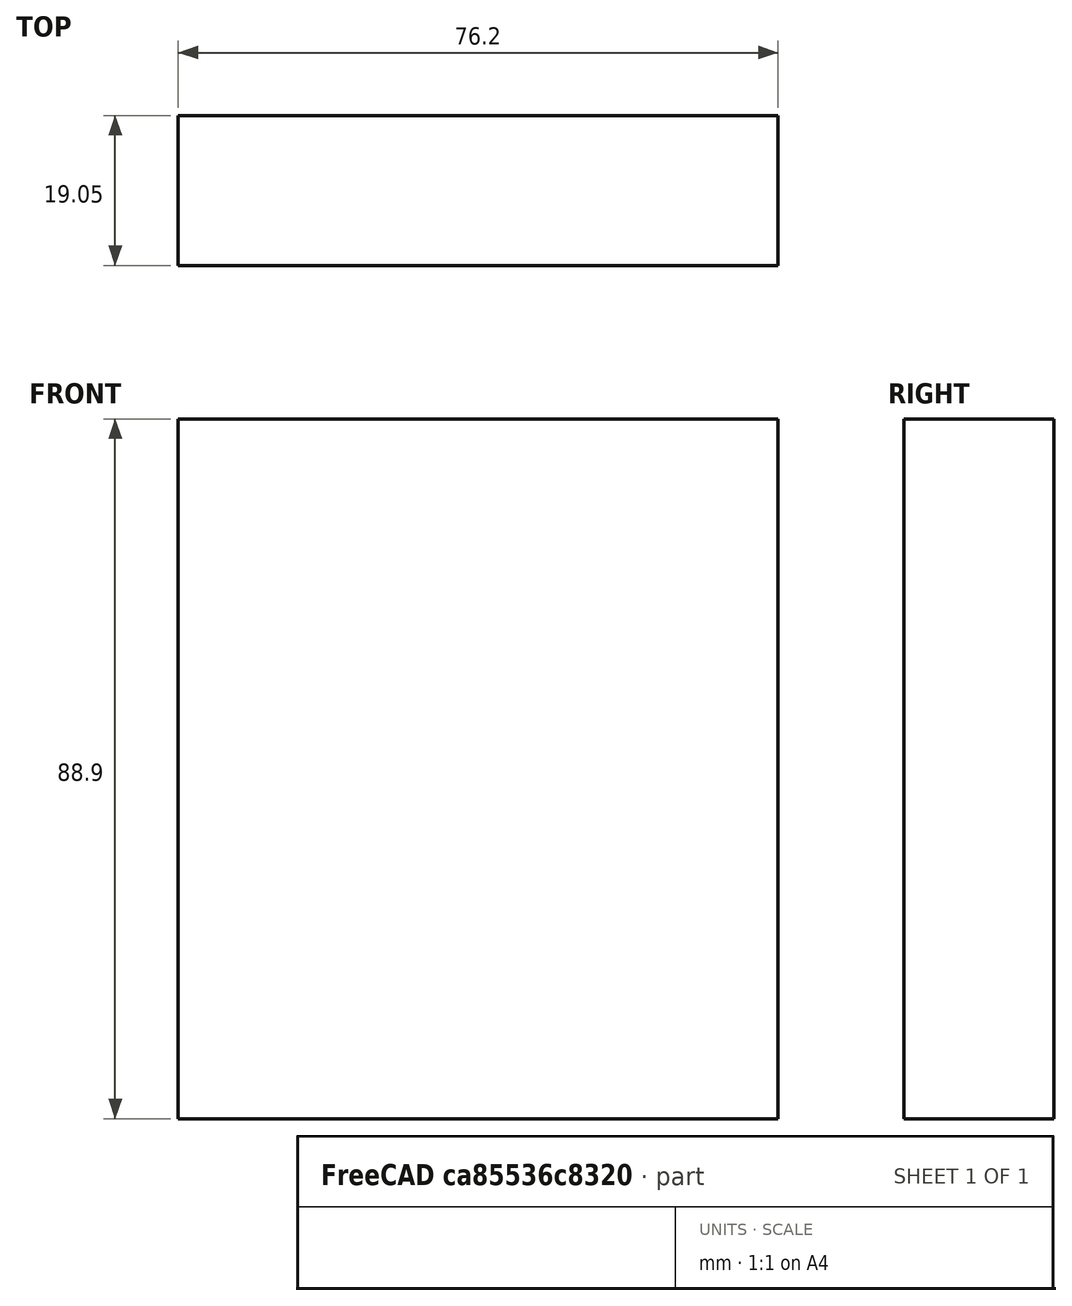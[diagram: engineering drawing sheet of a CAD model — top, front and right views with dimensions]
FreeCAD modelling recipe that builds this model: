
FCSTD DOCUMENT  (FreeCAD 0.20R29603 (Git))
Label: fence_insert
License: All rights reserved
LicenseURL: http://en.wikipedia.org/wiki/All_rights_reserved
objects: TechDraw::DrawProjGroupItem×3, TechDraw::DrawViewDimension×3, Sketcher::SketchObject×1, PartDesign::Pad×1, PartDesign::Body×1, TechDraw::DrawSVGTemplate×1, TechDraw::DrawProjGroup×1, TechDraw::DrawPage×1
note: 4 computed .brp shape members not serialized (recipe doc carries the construction recipe); baked Part::Feature solids carry a one-line shape summary decoded from their .brp

FEATURE [Sketcher::SketchObject] Sketch
  FullyConstrained = true
  MapMode = 5
  Placement = pos=(0,0,0) rot=(1,0,0;1.5708rad)
  Support = -> [XZ_Plane]
  sketch-geometry (5):
    g0: LineSegment StartX=-38.1 StartY=44.45 StartZ=0 EndX=-38.1 EndY=-44.45 EndZ=0
    g1: LineSegment StartX=-38.1 StartY=-44.45 StartZ=0 EndX=38.1 EndY=-44.45 EndZ=0
    g2: LineSegment StartX=38.1 StartY=-44.45 StartZ=0 EndX=38.1 EndY=44.45 EndZ=0
    g3: LineSegment StartX=38.1 StartY=44.45 StartZ=0 EndX=-38.1 EndY=44.45 EndZ=0
    g4: GeomPoint X=0 Y=0 Z=0
  constraints (12):
    c: Coincident(g0,g1)
    c: Coincident(g1,g2)
    c: Coincident(g2,g3)
    c: Coincident(g3,g0)
    c: Horizontal(g1)
    c: Horizontal(g3)
    c: Vertical(g0)
    c: Vertical(g2)
    c: Symmetric(g1,g0,g4)
    c: Distance(g3) = 76.2
    c: Distance(g2) = 88.9
    c: Coincident(g4,g-1)
FEATURE [PartDesign::Pad] Pad
  Direction = (0,-1,-2e-16)
  Length = 19.05
  Length2 = 10
  Placement = pos=(0,0,0) rot=(1,0,0;1.5708rad)
  Profile = -> Sketch
  ReferenceAxis = -> Sketch [N_Axis]
  Type = 0
FEATURE [PartDesign::Body] Body
  Group = -> [Sketch,Pad]
  Origin = -> Origin
  Tip = -> Pad
FEATURE [TechDraw::DrawSVGTemplate] Template
  Height = 297
  Orientation = 1
  Width = 420
FEATURE [TechDraw::DrawProjGroupItem] ProjItem  label="Front"
  CoarseView = false
  Direction = (0,-1,0)
  Focus = 100
  HardHidden = false
  IsoCount = 0
  IsoHidden = false
  IsoVisible = false
  LockPosition = true
  Perspective = false
  Rotation = 0
  RotationVector = (1,0,0)
  Scale = 0.7
  ScaleType = 2
  SeamHidden = false
  SeamVisible = true
  SmoothHidden = false
  SmoothVisible = true
  Source = -> [Body]
  Type = 0
  X = 0
  XDirection = (1,0,0)
  Y = 0
FEATURE [TechDraw::DrawProjGroupItem] ProjItem001  label="Left"
  CoarseView = false
  Direction = (-1,-1e-16,0)
  Focus = 100
  HardHidden = false
  IsoCount = 0
  IsoHidden = false
  IsoVisible = false
  LockPosition = false
  Perspective = false
  Rotation = 0
  RotationVector = (1,0,0)
  Scale = 0.7
  ScaleType = 2
  SeamHidden = false
  SeamVisible = true
  SmoothHidden = false
  SmoothVisible = true
  Source = -> [Body]
  Type = 1
  X = 93.1118
  XDirection = (1e-16,-1,0)
  Y = 0
FEATURE [TechDraw::DrawProjGroupItem] ProjItem002  label="FrontTopRight"
  CoarseView = false
  Direction = (0.57735,-0.57735,0.57735)
  Focus = 100
  HardHidden = false
  IsoCount = 0
  IsoHidden = false
  IsoVisible = false
  LockPosition = false
  Perspective = false
  Rotation = 0
  RotationVector = (1,0,0)
  Scale = 0.7
  ScaleType = 2
  SeamHidden = false
  SeamVisible = true
  SmoothHidden = false
  SmoothVisible = true
  Source = -> [Body]
  Type = 7
  X = 176.287
  XDirection = (0.707107,0.707107,0)
  Y = 75.4285
FEATURE [TechDraw::DrawProjGroup] ProjGroup
  Anchor = -> ProjItem
  AutoDistribute = false
  LockPosition = false
  ProjectionType = 0
  Rotation = 0
  Scale = 0.7
  ScaleType = 0
  Source = -> [Body]
  Views = -> [ProjItem,ProjItem001,ProjItem002]
  X = 176.286
  Y = 155.839
  spacingX = 15.0812
  spacingY = 15.0812
FEATURE [TechDraw::DrawViewDimension] Dimension
  AngleOverride = false
  Arbitrary = false
  ArbitraryTolerances = false
  EqualTolerance = true
  ExtensionAngle = 0
  FormatSpec = %.2w
  FormatSpecOverTolerance = %+.2w
  FormatSpecUnderTolerance = %+.2w
  Inverted = false
  LineAngle = 0
  LockPosition = false
  MeasureType = 1
  OverTolerance = 0
  References2D = -> [ProjItem]
  Rotation = 0
  Scale = 0.7
  ScaleType = 0
  TheoreticalExact = false
  Type = 1
  UnderTolerance = 0
  X = 2.09361
  Y = 46.2564
FEATURE [TechDraw::DrawViewDimension] Dimension001
  AngleOverride = false
  Arbitrary = false
  ArbitraryTolerances = false
  EqualTolerance = true
  ExtensionAngle = 0
  FormatSpec = %.2w
  FormatSpecOverTolerance = %+.2w
  FormatSpecUnderTolerance = %+.2w
  Inverted = false
  LineAngle = 0
  LockPosition = false
  MeasureType = 1
  OverTolerance = 0
  References2D = -> [ProjItem]
  Rotation = 0
  Scale = 0.7
  ScaleType = 0
  TheoreticalExact = false
  Type = 2
  UnderTolerance = 0
  X = -41.8487
  Y = 5.7201
FEATURE [TechDraw::DrawViewDimension] Dimension002
  AngleOverride = false
  Arbitrary = false
  ArbitraryTolerances = false
  EqualTolerance = true
  ExtensionAngle = 0
  FormatSpec = %.2w
  FormatSpecOverTolerance = %+.2w
  FormatSpecUnderTolerance = %+.2w
  Inverted = false
  LineAngle = 0
  LockPosition = false
  MeasureType = 1
  OverTolerance = 0
  References2D = -> [ProjItem001]
  Rotation = 0
  Scale = 0.7
  ScaleType = 0
  TheoreticalExact = false
  Type = 1
  UnderTolerance = 0
  X = 21.4595
  Y = 45.2095
FEATURE [TechDraw::DrawPage] Page
  KeepUpdated = true
  NextBalloonIndex = 1
  ProjectionType = 0
  Scale = 0.7
  Template = -> Template
  Views = -> [ProjGroup,Dimension,Dimension001,Dimension002]
